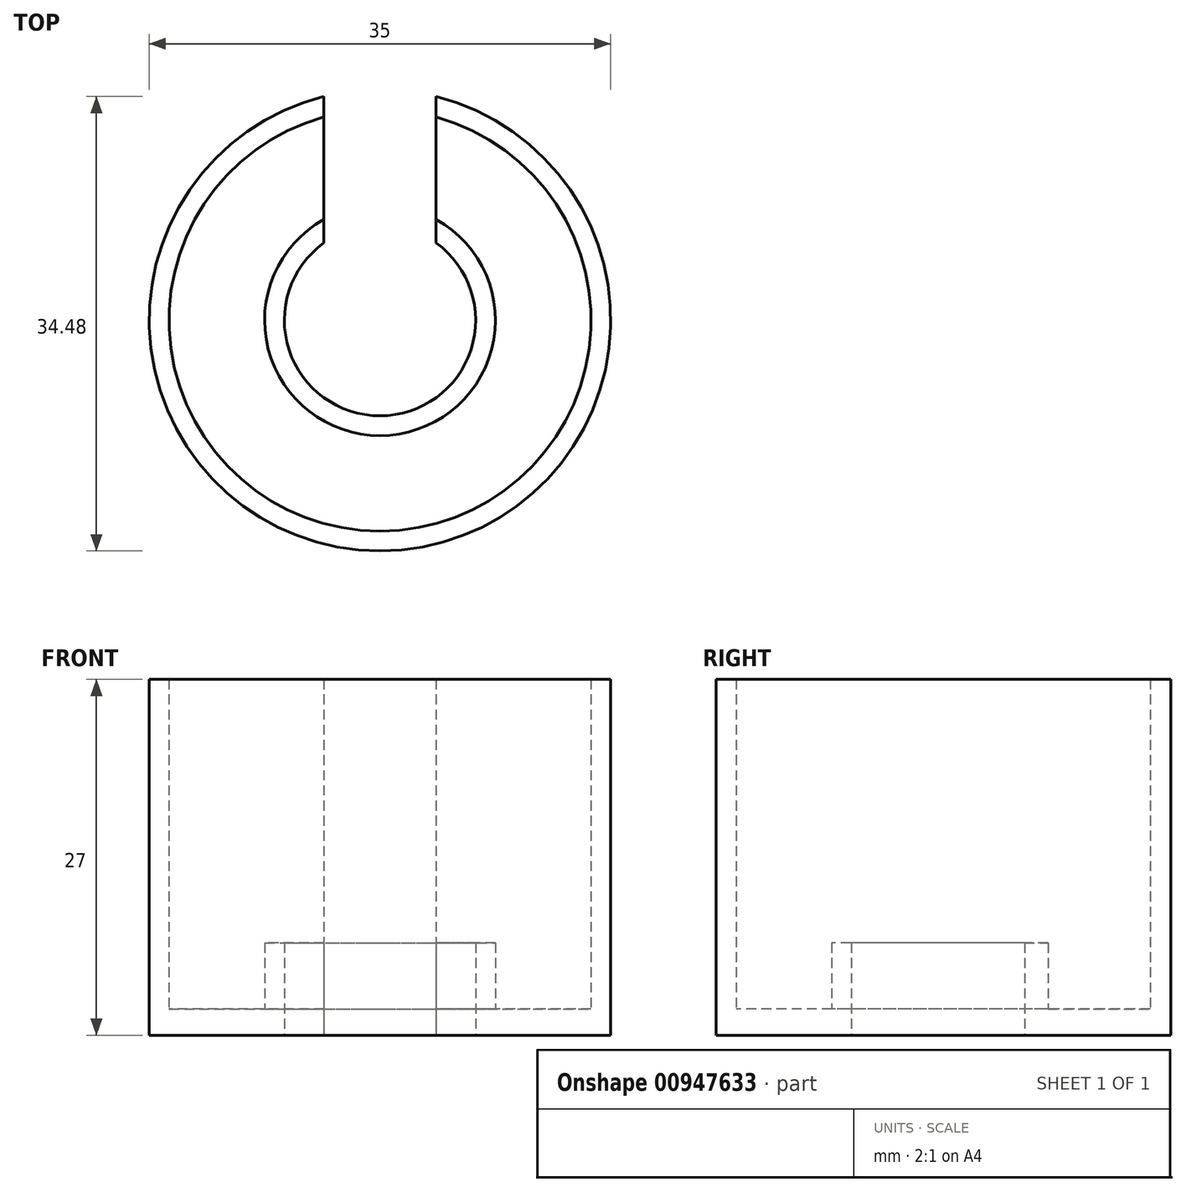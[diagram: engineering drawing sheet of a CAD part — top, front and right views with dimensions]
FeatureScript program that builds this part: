
annotation { "Feature Type Name" : "Feature", "Feature Type Description" : "" }
export const myFeature = defineFeature(function(context is Context, id is Id, definition is map)
    precondition{}
    {
        {
            var Q0;
            Q0=qCreatedBy(makeId("Top.planeOp"),FACE);
            var sketch = newSketch(context, id + "F0", { "sketchPlane" : qUnion([Q0])});
            skCircle(sketch, "E0", {"center": v(0, 0) * mm, "radius": 17.5 * mm});
            skCircle(sketch, "E1", {"center": v(0, 0) * mm, "radius": 7.25 * mm});
            skSolve(sketch);
        }
        {
            var Q0;
            Q0=makeQuery(id+"F0.imprint","IMPRINT",FACE,{"disambiguationData":[TD([[makeQuery(id+"F0.imprint","IMPRINT",EDGE,{"derivedFrom":sQuery(id+"F0.wireOp",EDGE,"E0")}),1.0]])]});
            extrude(context, id + "F1", {"entities" : qUnion([Q0]), "depth" : 2 * mm, "offsetDistance" : 25 * mm});
        }
        {
            var Q0;
            Q0=makeQuery(id+"F1.opExtrude","CAP_FACE",FACE,{"disambiguationData":[OSD([sQuery(id+"F0.wireOp",EDGE,"E0"),sQuery(id+"F0.wireOp",EDGE,"E1")])],"isStart":false});
            var sketch = newSketch(context, id + "F2", { "sketchPlane" : qUnion([Q0])});
            skCircle(sketch, "E2.0", {"center": v(0, 0) * mm, "radius": 17.5 * mm});
            skCircle(sketch, "E3.0", {"center": v(0, 0) * mm, "radius": 7.25 * mm});
            skCircle(sketch, "E4.0", {"center": v(0, 0) * mm, "radius": 16 * mm});
            skCircle(sketch, "E5.0", {"center": v(0, 0) * mm, "radius": 8.75 * mm});
            skSolve(sketch);
        }
        {
            var Q0;
            Q0=makeQuery(id+"F2.imprint","IMPRINT",FACE,{"disambiguationData":[TD([[makeQuery(id+"F2.imprint","IMPRINT",EDGE,{"derivedFrom":sQuery(id+"F2.wireOp",EDGE,"E3.0")}),-1.0]])]});
            extrude(context, id + "F3", {"entities" : qUnion([Q0]), "operationType" : NewBodyOperationType.ADD, "depth" : 5 * mm, "offsetDistance" : 25 * mm});
        }
        {
            var Q0;
            Q0=makeQuery(id+"F2.imprint","IMPRINT",FACE,{"disambiguationData":[TD([[makeQuery(id+"F2.imprint","IMPRINT",EDGE,{"derivedFrom":sQuery(id+"F2.wireOp",EDGE,"E2.0")}),1.0]])]});
            extrude(context, id + "F4", {"entities" : qUnion([Q0]), "operationType" : NewBodyOperationType.ADD, "depth" : 25 * mm, "offsetDistance" : 25 * mm});
        }
        {
            var Q0;
            Q0=qCreatedBy(makeId("Top.planeOp"),FACE);
            var sketch = newSketch(context, id + "F5", { "sketchPlane" : qUnion([Q0])});
            skLineSegment(sketch, "E6.bottom", {"start": v(-4.25, 0) * mm, "end": v(4.25, 0) * mm});
            skLineSegment(sketch, "E6.top", {"start": v(-4.25, 17.5) * mm, "end": v(4.25, 17.5) * mm});
            skLineSegment(sketch, "E6.left", {"start": v(-4.25, 0) * mm, "end": v(-4.25, 17.5) * mm});
            skLineSegment(sketch, "E6.right", {"start": v(4.25, 0) * mm, "end": v(4.25, 17.5) * mm});
            skPoint(sketch, "E7", {"position": v(0, 0) * mm});
            skPoint(sketch, "E8", {"position": v(0, 17.5) * mm});
            skCircle(sketch, "E9.0", {"center": v(0, 0) * mm, "radius": 17.5 * mm, "construction": true});
            skSolve(sketch);
        }
        {
            var Q0;
            Q0 = qSketchRegion(id + "F5", true);
            extrude(context, id + "F6", {"entities" : qUnion([Q0]), "operationType" : NewBodyOperationType.REMOVE, "endBound" : BoundingType.UP_TO_NEXT, "depth" : 25 * mm, "offsetDistance" : 25 * mm});
        }
    });
